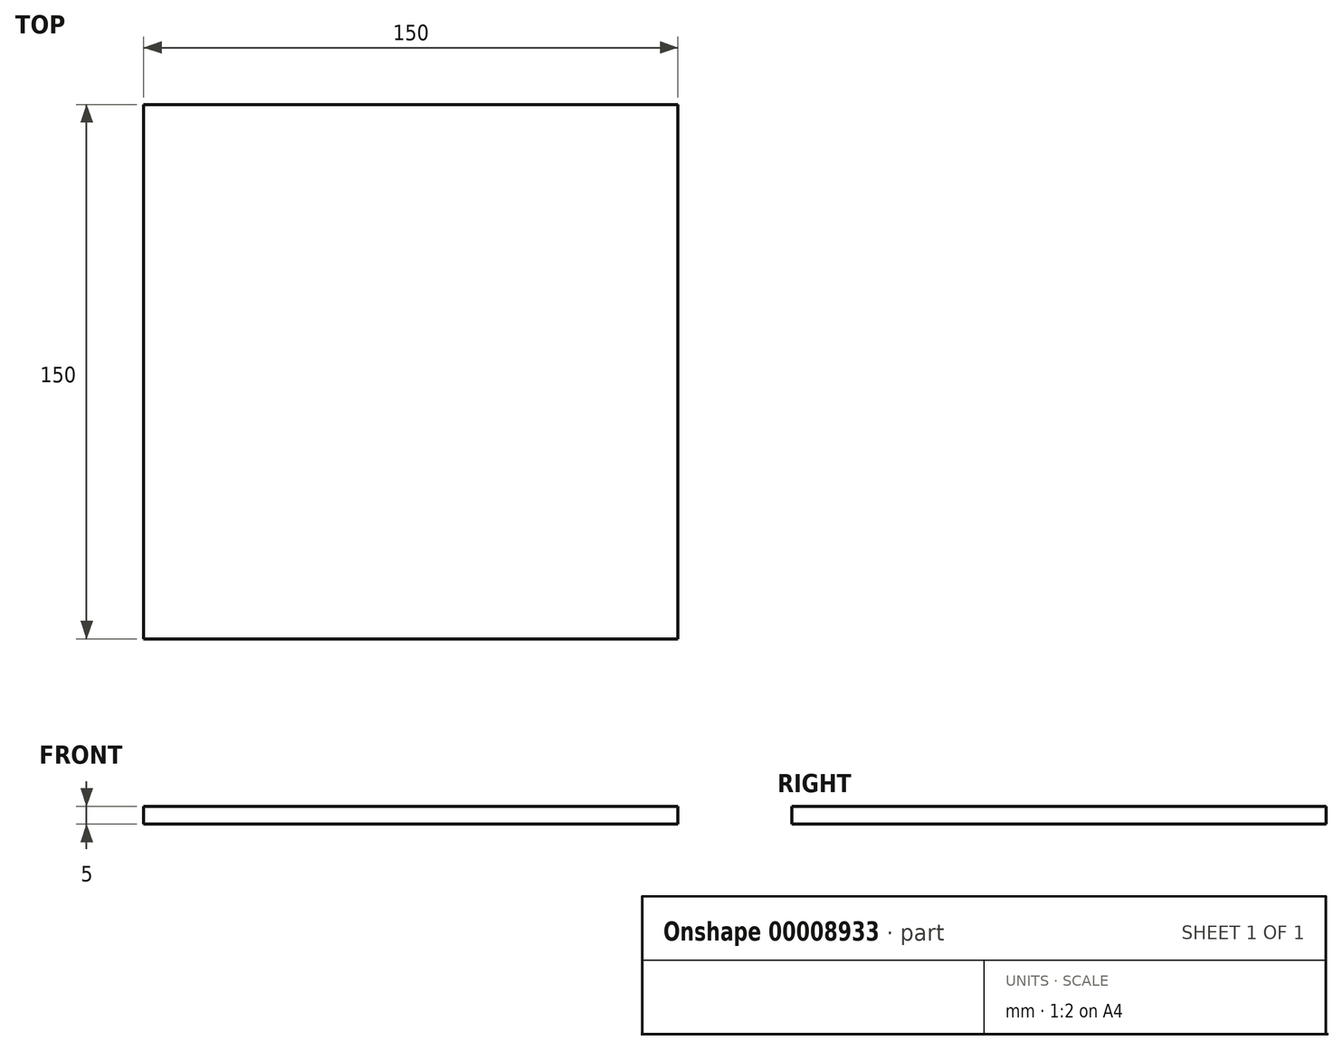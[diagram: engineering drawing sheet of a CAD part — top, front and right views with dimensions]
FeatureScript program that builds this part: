
annotation { "Feature Type Name" : "Feature", "Feature Type Description" : "" }
export const myFeature = defineFeature(function(context is Context, id is Id, definition is map)
    precondition{}
    {
        {
            var Q0;
            Q0=qCreatedBy(makeId("Top.planeOp"),FACE);
            var sketch = newSketch(context, id + "F0", { "sketchPlane" : qUnion([Q0])});
            skLineSegment(sketch, "E0.rect.bottom", {"start": v(75, 75) * mm, "end": v(-75, 75) * mm});
            skLineSegment(sketch, "E0.rect.top", {"start": v(75, -75) * mm, "end": v(-75, -75) * mm});
            skLineSegment(sketch, "E0.rect.left", {"start": v(75, 75) * mm, "end": v(75, -75) * mm});
            skLineSegment(sketch, "E0.rect.right", {"start": v(-75, 75) * mm, "end": v(-75, -75) * mm});
            skPoint(sketch, "E0.rect.middle", {"position": v(0, 0) * mm});
            skSolve(sketch);
        }
        {
            var Q0;
            Q0 = qSketchRegion(id + "F0", true);
            extrude(context, id + "F1", {"entities" : qUnion([Q0]), "depth" : 5 * mm});
        }
    });
